# Revit family: protivipozarnae_stora_firetechnics-h_gorizontalnay
name_source: partatom
category: Двери
revit_build: Autodesk Revit 2018 (Build: 20170223_1515(x64)
units: mm (PartAtom-declared; Revit-internal decimal feet)

## family parameters
Всегда вертикально = Нет
На основе рабочей плоскости = Да
Общий = Нет
При загрузке вырезать с полостями = Нет
Точка расчета площади = Нет

## types (1)
- Противопожарная штора Firetechnics-H "Горизонтальная"
    ADSK_URL страницы изделия = https://www.fire-tec.ru
    ADSK_Завод-изготовитель = Firetechnics
    ADSK_Наименование = Противопожарная штора Firetechnics-H "Горизонтальная"
    ADSK_Предел огнестойкости = EI60
    ADSK_Размер_Высота = 3000 мм
    ADSK_Размер_Ширина = 3000 мм
    URL = https://www.fire-tec.ru
    Аналитическая конструкция = <Нет>
    Высота = 3000 мм
    Высота верхнего короба = 200 мм
    Высота направляющей = 60 мм
    Высота нижнего короба = 150 мм
    Высота полотна = 1 мм
    Высота рабочего короба = 175 мм
    Изготовитель = Firetechnics
    Материал корпуса = Сталь_оцинкованная_листовая Firetechnics
    Материал нижнего корпуса = Сталь_оцинкованная_листовая_2мм_Firetechnics
    Материал полотна = Полотно
    Отметка по умолчанию = 1219 мм
    Ширина = 3000 мм
    Ширина вернего короба = 220 мм
    Ширина направляющей = 60 мм
    Ширина нижнего короба = 150 мм

## geometry (parser evidence)
native form markers: Blend x2
no freeform markers — native parametric forms only
